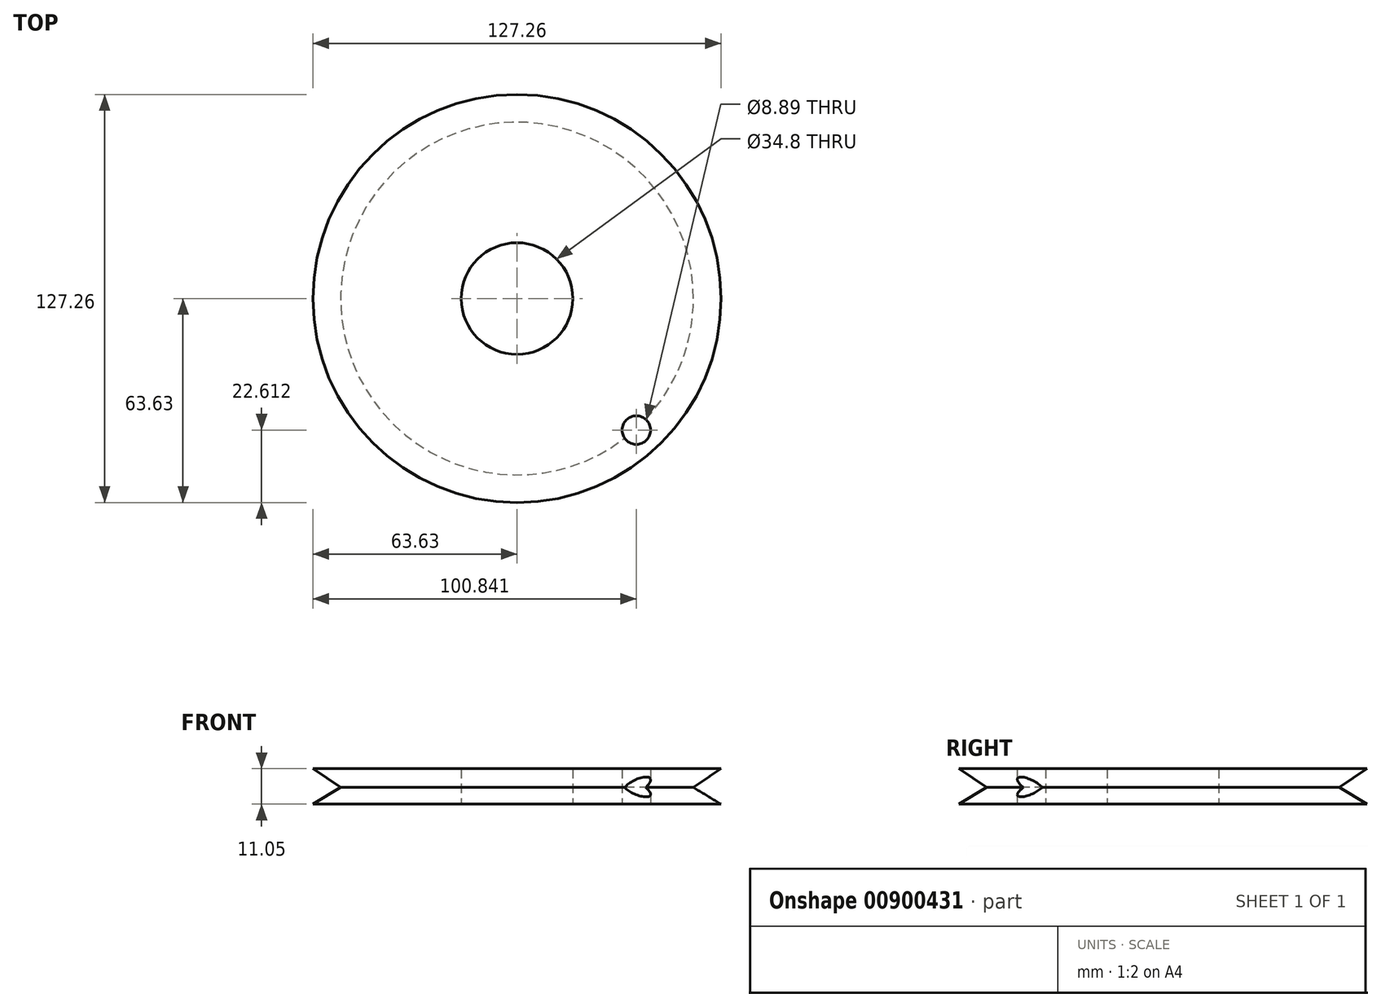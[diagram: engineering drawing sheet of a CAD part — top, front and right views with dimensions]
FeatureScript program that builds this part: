
annotation { "Feature Type Name" : "Feature", "Feature Type Description" : "" }
export const myFeature = defineFeature(function(context is Context, id is Id, definition is map)
    precondition{}
    {
        {
            var Q0;
            Q0=qCreatedBy(makeId("Front.planeOp"),FACE);
            var sketch = newSketch(context, id + "F0", { "sketchPlane" : qUnion([Q0])});
            skLineSegment(sketch, "E0", {"start": v(0, 0) * mm, "end": v(-63.63, 0) * mm});
            skLineSegment(sketch, "E1", {"start": v(-63.63, 0) * mm, "end": v(-55, 5.2) * mm});
            skLineSegment(sketch, "E2", {"start": v(-55, 5.2) * mm, "end": v(-63.63, 11.05) * mm});
            skLineSegment(sketch, "E3", {"start": v(-63.63, 11.05) * mm, "end": v(0, 11.05) * mm});
            skLineSegment(sketch, "E4", {"start": v(0, 11.05) * mm, "end": v(0, 0) * mm});
            skSolve(sketch);
        }
        {
            var Q0;
            Q0=makeQuery(id+"F0.imprint","IMPRINT",FACE,{"disambiguationData":[TD([[makeQuery(id+"F0.imprint","IMPRINT",EDGE,{"derivedFrom":sQuery(id+"F0.wireOp",EDGE,"E0")}),-1.0]])]});
            var Q1;
            Q1=sQuery(id+"F0.wireOp",EDGE,"E4");
            revolve(context, id + "F1", {"surfaceOperationType" : NewSurfaceOperationType.NEW, "entities" : qUnion([Q0]), "axis" : qUnion([Q1]), "revolveType" : RevolveType.FULL});
        }
        {
            var Q0;
            Q0=makeQuery(id+"F1.opRevolve","SWEPT_FACE",FACE,{"disambiguationData":[OSD([sQuery(id+"F0.wireOp",EDGE,"E0")])]});
            var sketch = newSketch(context, id + "F2", { "sketchPlane" : qUnion([Q0])});
            skCircle(sketch, "E5", {"center": v(37.21, 41.02) * mm, "radius": 4.44 * mm});
            skSolve(sketch);
        }
        {
            var Q0;
            Q0=makeQuery(id+"F2.imprint","IMPRINT",FACE,{"disambiguationData":[TD([[makeQuery(id+"F2.imprint","IMPRINT",EDGE,{"derivedFrom":sQuery(id+"F2.wireOp",EDGE,"E5")}),1.0]])]});
            extrude(context, id + "F3", {"entities" : qUnion([Q0]), "operationType" : NewBodyOperationType.REMOVE, "oppositeDirection" : true, "depth" : 25.4 * mm, "offsetDistance" : 25.4 * mm});
        }
        {
            var Q0;
            Q0=makeQuery(id+"F1.opRevolve","SWEPT_FACE",FACE,{"disambiguationData":[OSD([sQuery(id+"F0.wireOp",EDGE,"E0")])]});
            var sketch = newSketch(context, id + "F4", { "sketchPlane" : qUnion([Q0])});
            skCircle(sketch, "E6", {"center": v(0, 0) * mm, "radius": 17.4 * mm});
            skSolve(sketch);
        }
        {
            var Q0;
            Q0=makeQuery(id+"F4.imprint","IMPRINT",FACE,{"disambiguationData":[TD([[makeQuery(id+"F4.imprint","IMPRINT",EDGE,{"derivedFrom":sQuery(id+"F4.wireOp",EDGE,"E6")}),1.0]])]});
            extrude(context, id + "F5", {"entities" : qUnion([Q0]), "operationType" : NewBodyOperationType.REMOVE, "oppositeDirection" : true, "depth" : 25.4 * mm, "offsetDistance" : 25.4 * mm});
        }
    });
